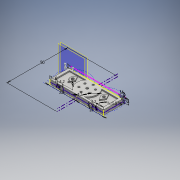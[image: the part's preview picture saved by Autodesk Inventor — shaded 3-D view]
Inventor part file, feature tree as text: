
AUTODESK INVENTOR PART (.ipt)
format: ipt  version: 2016 (Build 200138000, 138)  size: 313,344 bytes
history: native  units: mm
features: extrude x6, other x5, hole x2, fillet x2, sketch x1
ambient origin geometry x8: Origin, YZ Plane, XZ Plane, XY Plane, X Axis, Y Axis, Z Axis, Center Point
bodies: Body1 (feature_tree)
feature tree (16):
  other  "構築線"
  extrude  "押し出し11"  Depth=17.0mm
  other  "作業平面2"
  extrude  "押し出し16"  Depth=5.6mm
  other  "固定穴"
  extrude  "押し出し19"  Depth=10.0mm
  extrude  "押し出し20"  Depth=25.0mm
  extrude  "押し出し21"  Depth=8.6mm
  other  "ねじ穴+固定(基板)"
  hole  "ねじ穴(基板)"  [1 undecoded]
  extrude  "押し出し22"  Depth=20.1mm
  fillet  "フィレット1"  [1 undecoded]
  fillet  "フィレット2"  Radius=25.0mm
  other  "作業平面1"
  hole  "穴4"  [1 undecoded]
  sketch  "スケッチ12"
note: 3 required parameter values undecoded (feature->parameter linkage not recoverable at this tier; creation-order binding heuristic only, values carry confidence <= 0.55)
